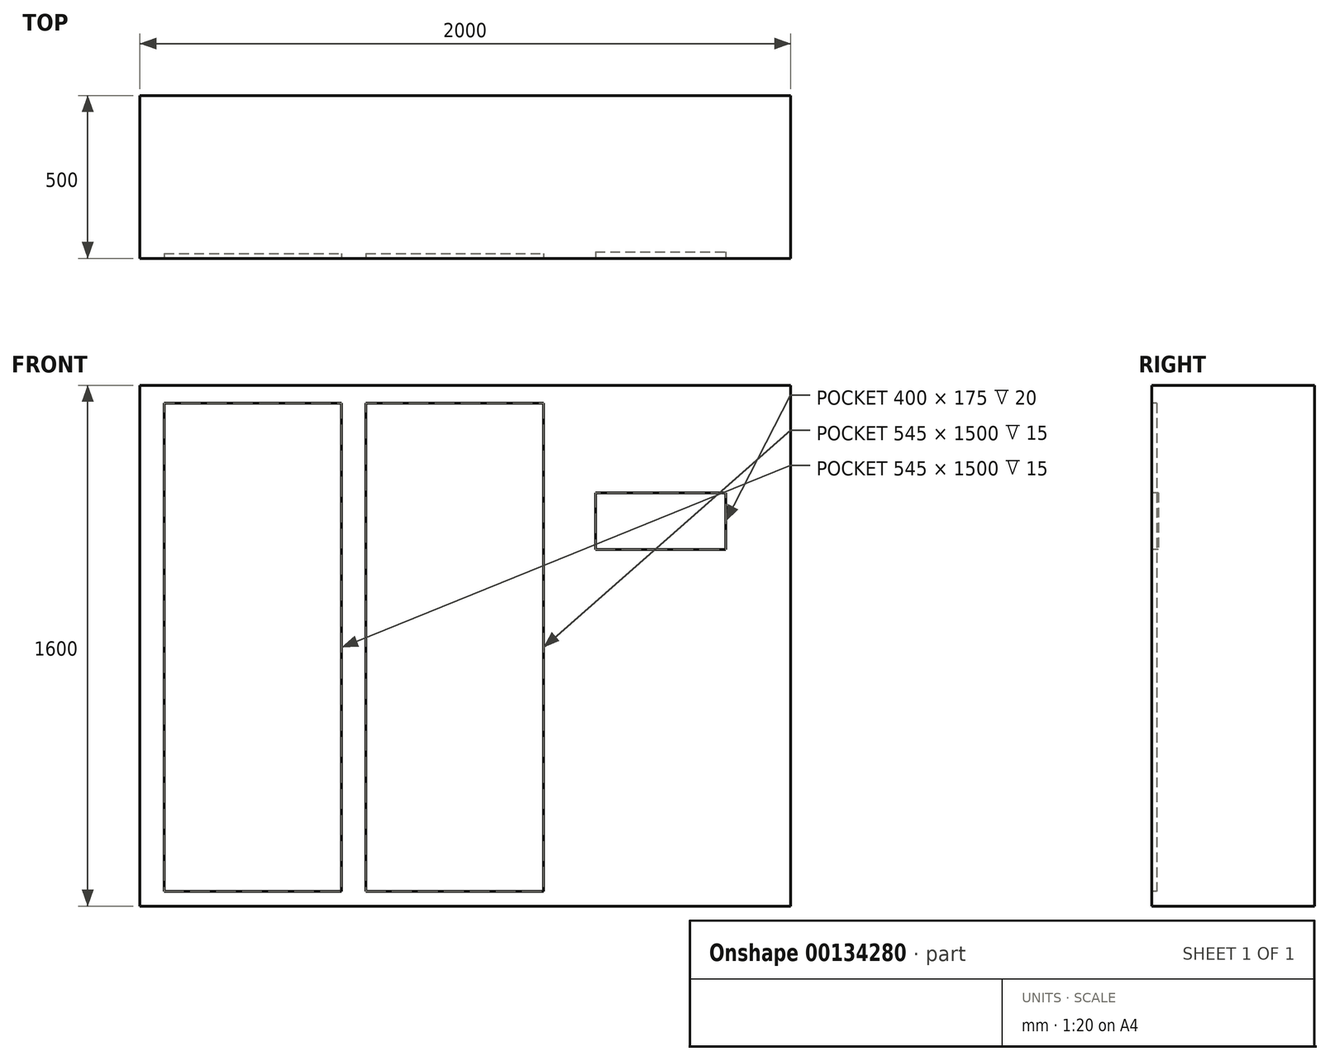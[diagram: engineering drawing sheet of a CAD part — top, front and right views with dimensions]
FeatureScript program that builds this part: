
annotation { "Feature Type Name" : "Feature", "Feature Type Description" : "" }
export const myFeature = defineFeature(function(context is Context, id is Id, definition is map)
    precondition{}
    {
        {
            var Q0;
            Q0=qCreatedBy(makeId("Front.planeOp"),FACE);
            var sketch = newSketch(context, id + "F0", { "sketchPlane" : qUnion([Q0])});
            skLineSegment(sketch, "E0.bottom", {"start": v(0, 0) * mm, "end": v(2000, 0) * mm});
            skLineSegment(sketch, "E0.top", {"start": v(0, 1600) * mm, "end": v(2000, 1600) * mm});
            skLineSegment(sketch, "E0.left", {"start": v(0, 0) * mm, "end": v(0, 1600) * mm});
            skLineSegment(sketch, "E0.right", {"start": v(2000, 0) * mm, "end": v(2000, 1600) * mm});
            skSolve(sketch);
        }
        {
            var Q0;
            Q0 = qSketchRegion(id + "F0", true);
            extrude(context, id + "F1", {"entities" : qUnion([Q0]), "depth" : 500 * mm});
        }
        {
            var Q0;
            Q0=makeQuery(id+"F1.opExtrude","CAP_FACE",FACE,{"disambiguationData":[OSD([sQuery(id+"F0.wireOp",EDGE,"E0.bottom"),sQuery(id+"F0.wireOp",EDGE,"E0.top"),sQuery(id+"F0.wireOp",EDGE,"E0.left"),sQuery(id+"F0.wireOp",EDGE,"E0.right")])],"isStart":false});
            var sketch = newSketch(context, id + "F2", { "sketchPlane" : qUnion([Q0])});
            skLineSegment(sketch, "E1.bottom", {"start": v(1400, 1270) * mm, "end": v(1800, 1270) * mm});
            skLineSegment(sketch, "E1.top", {"start": v(1400, 1095) * mm, "end": v(1800, 1095) * mm});
            skLineSegment(sketch, "E1.left", {"start": v(1400, 1270) * mm, "end": v(1400, 1095) * mm});
            skLineSegment(sketch, "E1.right", {"start": v(1800, 1270) * mm, "end": v(1800, 1095) * mm});
            skSolve(sketch);
        }
        {
            var Q0;
            Q0 = qSketchRegion(id + "F2", true);
            extrude(context, id + "F3", {"entities" : qUnion([Q0]), "operationType" : NewBodyOperationType.REMOVE, "oppositeDirection" : true, "depth" : 20 * mm});
        }
        {
            var Q0;
            Q0=makeQuery(id+"F1.opExtrude","CAP_FACE",FACE,{"disambiguationData":[OSD([sQuery(id+"F0.wireOp",EDGE,"E0.bottom"),sQuery(id+"F0.wireOp",EDGE,"E0.top"),sQuery(id+"F0.wireOp",EDGE,"E0.left"),sQuery(id+"F0.wireOp",EDGE,"E0.right")])],"isStart":false});
            var sketch = newSketch(context, id + "F4", { "sketchPlane" : qUnion([Q0])});
            skLineSegment(sketch, "E2.bottom", {"start": v(75, 1545) * mm, "end": v(620, 1545) * mm});
            skLineSegment(sketch, "E2.top", {"start": v(75, 45) * mm, "end": v(620, 45) * mm});
            skLineSegment(sketch, "E2.left", {"start": v(75, 1545) * mm, "end": v(75, 45) * mm});
            skLineSegment(sketch, "E2.right", {"start": v(620, 1545) * mm, "end": v(620, 45) * mm});
            skLineSegment(sketch, "E3.bottom", {"start": v(695, 1545) * mm, "end": v(1240, 1545) * mm});
            skLineSegment(sketch, "E3.top", {"start": v(695, 45) * mm, "end": v(1240, 45) * mm});
            skLineSegment(sketch, "E3.left", {"start": v(695, 1545) * mm, "end": v(695, 45) * mm});
            skLineSegment(sketch, "E3.right", {"start": v(1240, 1545) * mm, "end": v(1240, 45) * mm});
            skSolve(sketch);
        }
        {
            var Q0;
            Q0 = qSketchRegion(id + "F4", true);
            extrude(context, id + "F5", {"entities" : qUnion([Q0]), "operationType" : NewBodyOperationType.REMOVE, "oppositeDirection" : true, "depth" : 15 * mm});
        }
    });
